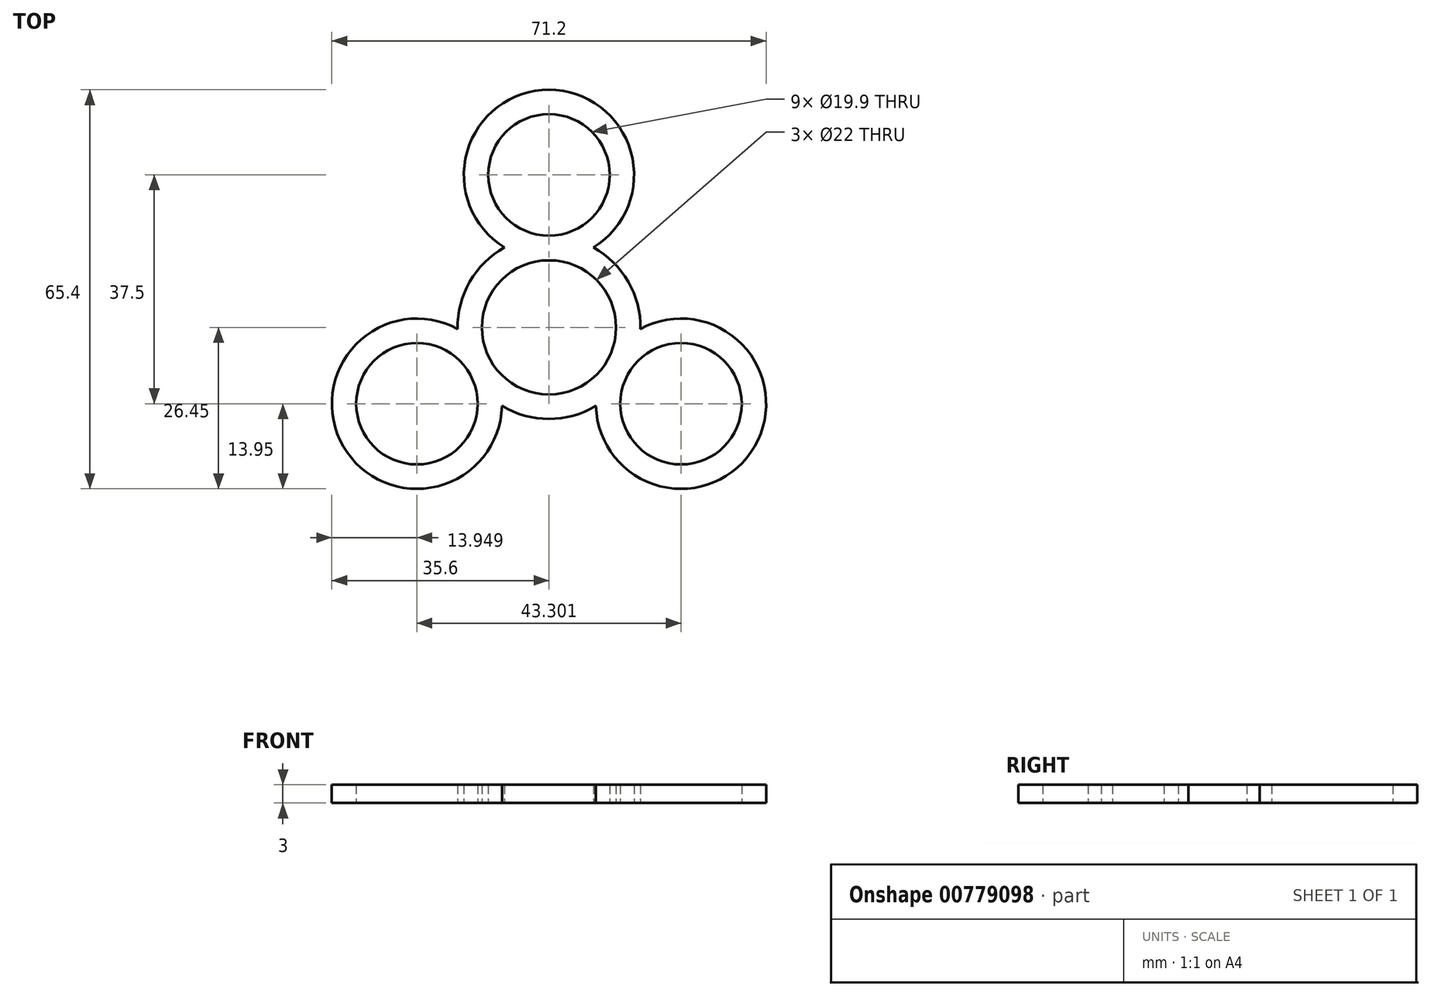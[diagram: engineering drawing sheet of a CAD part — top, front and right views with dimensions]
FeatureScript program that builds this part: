
annotation { "Feature Type Name" : "Feature", "Feature Type Description" : "" }
export const myFeature = defineFeature(function(context is Context, id is Id, definition is map)
    precondition{}
    {
        {
            var Q0;
            Q0=qCreatedBy(makeId("Top.planeOp"),FACE);
            var sketch = newSketch(context, id + "F0", { "sketchPlane" : qUnion([Q0])});
            skArc(sketch, "E0", {"start": v(9.53, 5.5) * mm, "mid": v(0, 11) * mm, "end": v(-9.53, 5.5) * mm});
            skArc(sketch, "E1", {"start": v(-7.3, 13.1) * mm, "mid": v(-10.52, 10.7) * mm, "end": v(-13, 7.5) * mm});
            skLineSegment(sketch, "E2", {"start": v(0, 0) * mm, "end": v(0, 15.05) * mm});
            skCircle(sketch, "E3", {"center": v(0, 25) * mm, "radius": 9.95 * mm});
            skArc(sketch, "E4", {"start": v(7.3, 13.1) * mm, "mid": v(0, 38.95) * mm, "end": v(-7.3, 13.1) * mm});
            skArc(sketch, "E5.trimOffspring", {"start": v(13, 7.5) * mm, "mid": v(10.52, 10.7) * mm, "end": v(7.3, 13.1) * mm});
            skArc(sketch, "E6.1.0", {"start": v(-9.53, 5.5) * mm, "mid": v(-9.53, -5.5) * mm, "end": v(0, -11) * mm});
            skArc(sketch, "E6.1.1", {"start": v(-15, -0.24) * mm, "mid": v(-33.73, -19.47) * mm, "end": v(-7.7, -12.87) * mm});
            skCircle(sketch, "E6.1.2", {"center": v(-21.65, -12.5) * mm, "radius": 9.95 * mm});
            skArc(sketch, "E6.1.3", {"start": v(-7.7, -12.87) * mm, "mid": v(-4, -14.46) * mm, "end": v(0, -15) * mm});
            skArc(sketch, "E6.1.4", {"start": v(-13, 7.5) * mm, "mid": v(-14.52, 3.77) * mm, "end": v(-15, -0.24) * mm});
            skArc(sketch, "E6.2.0", {"start": v(0, -11) * mm, "mid": v(9.53, -5.5) * mm, "end": v(9.53, 5.5) * mm});
            skArc(sketch, "E6.2.1", {"start": v(7.7, -12.87) * mm, "mid": v(33.73, -19.48) * mm, "end": v(15, -0.24) * mm});
            skCircle(sketch, "E6.2.2", {"center": v(21.65, -12.5) * mm, "radius": 9.95 * mm});
            skArc(sketch, "E6.2.3", {"start": v(15, -0.24) * mm, "mid": v(14.52, 3.77) * mm, "end": v(13, 7.5) * mm});
            skArc(sketch, "E6.2.4", {"start": v(0, -15) * mm, "mid": v(4, -14.46) * mm, "end": v(7.7, -12.87) * mm});
            skSolve(sketch);
        }
        {
            var Q0;
            Q0=makeQuery(id+"F0.imprint","IMPRINT",FACE,{"disambiguationData":[TD([[makeQuery(id+"F0.imprint","IMPRINT",EDGE,{"derivedFrom":sQuery(id+"F0.wireOp",EDGE,"E1")}),1.0]])]});
            extrude(context, id + "F1", {"entities" : qUnion([Q0]), "depth" : 3 * mm, "offsetDistance" : 25 * mm});
        }
    });
